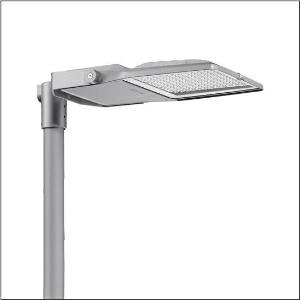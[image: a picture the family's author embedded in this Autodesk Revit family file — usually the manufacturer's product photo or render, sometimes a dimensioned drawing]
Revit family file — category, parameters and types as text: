
# Revit family: floodlight_fl_21_iq_midi___pl64_5xa7782e2e3a_fffa
name_source: partatom
category: Lighting Fixtures
units: mm (PartAtom-declared; Revit-internal decimal feet)

## family parameters
Cut with Voids When Loaded = No
Host = Face
Light Source = No
Part Type = Normal
Room Calculation Point = No
Round Connector Dimension = Use Diameter
Shared = No

## types (1)
- --- (1 x LED, 25930 lm, 208.1 W, 3000K)
    Apparent Load = 208 VA
    CIE Flux Codes = 28 80 98 100 100
    Color Rendering = 70
    Color Temperature = 3000K
    Default Elevation = 1800 mm
    Description = Floodlight FL 21 iQ midi, floodlight, primary light control with lens, of PMMA, primary optical cover: protective disc, of toughened safety glass, transparent, light distribution: PL64, light emission: direct distribution, installation type: surface-mounted, LED, High Power LED, rated luminous flux: 25.930lm, luminous efficacy: 125lm/W, light colour: 730, colour temperature: 3000K, control gear: ECG iQ, control: optimised constant luminous flux control (CLO 2.0), Desk-Remote (wireless, voltage-free reading and setting of iQ features in the workshop via application-optimized NFC function/RFID function), Smart-Wire, Night-Set, Temp-Guard, Auto-Match, Street-Remote, with terminal, 6-pole, mains connection: 220..240V, AC, 50/60Hz, start of lifetime: 208W, end of service life: 227W, reduction: 90W, luminaire housing, of diecast aluminium, powder-coated, Siteco® metallic grey (DB 702S), corrosivity category C5 mid according to DIN EN ISO 12944, sealing non-destructively replaceable, please order mast flange separately, mast bracket, of steel, galvanised, powder-coated, Siteco® metallic grey (DB 702S), protection rating (complete): IP66, insulation class (complete): insulation class II (safety insulation), certification: CE, protection symbol: D, impact resistance: IK08, permissible operating ambient temperature: -40..+40°C, permissible operating ambient temperature for outdoor applications: -40..+50°C, standard: DIN EN 12944, LABS conformity tested according to VDMA 24364:2018-05, packaging unit: 1 piece

Light Distribution: PL64
    Height = 76 mm
    Lamp = 1 x LED
    Lamp Light Flux = 25930 lm
    Lamp Power = 208.1 W
    Lamp count = 1
    Length = 657 mm
    Luminous efficacy = 125 lm/W
    Manufacturer = Siteco
    ModVariant = No
    Model = 5XA7782E2E3A
    Number of Poles = 1
    OnlyDefault = Yes
    Power Factor = 1
    Product Name = Floodlight FL 21 iQ midi | PL64
    Product group = floodlight | pylon annexe
    ProductGroupID = 6200
    Protection Class = Protection class II
    Protection Degree = IP 66
    RLX_Detail_Level = 1
    RLX_Emergency_Light_Flux = 0 lm
    RLX_Emergency_Type = 0
    RLX_Emergency_Type_DB = No
    RlxData = <blob elided: 153409 chars, md5=70562ad1>
    Socket = socket
    Standby Power = 0 W
    System Light Flux = 25930 lm
    System Power = 208 W
    Type Comments = factory setting: luminous flux: 100 % | dim-lin: 254 | 710 mA
    Type Image = l_1007123.jpg
    URL = http://relux.com
    VarID = @adj_055381
    Voltage = 0 V
    Weight = 0.00 kg
    Width = 442 mm

## geometry (parser evidence)
native form markers: Blend x4, Sweep x14
no freeform markers — native parametric forms only
